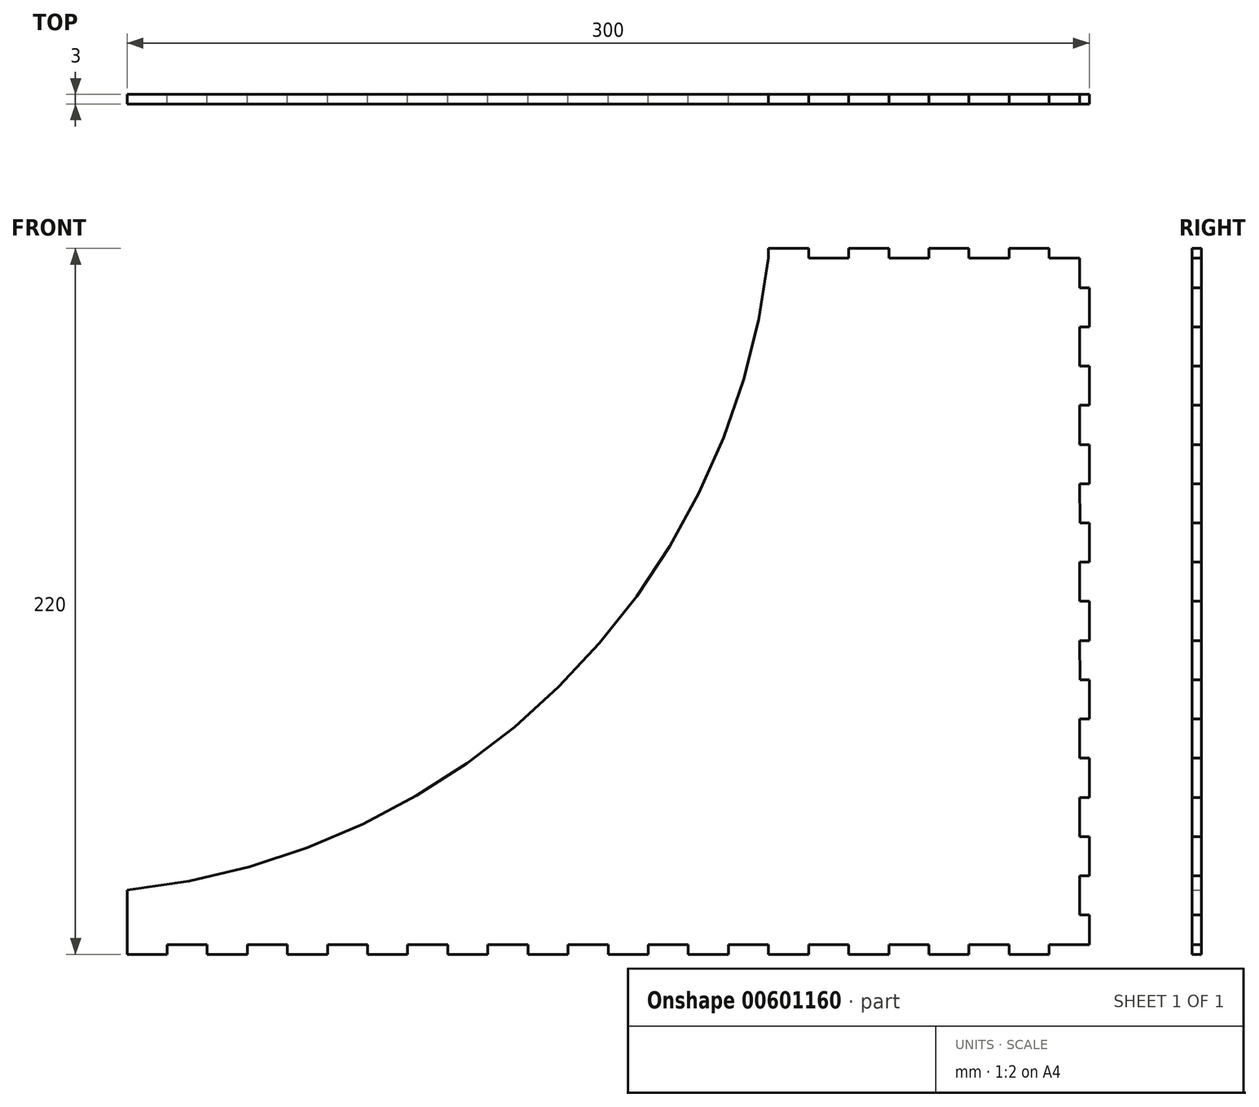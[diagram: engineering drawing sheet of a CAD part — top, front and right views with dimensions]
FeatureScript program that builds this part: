
annotation { "Feature Type Name" : "Feature", "Feature Type Description" : "" }
export const myFeature = defineFeature(function(context is Context, id is Id, definition is map)
    precondition{}
    {
        {
            var Q0;
            Q0=qCreatedBy(makeId("Front.planeOp"),FACE);
            var sketch = newSketch(context, id + "F0", { "sketchPlane" : qUnion([Q0])});
            skLineSegment(sketch, "E0.bottom", {"start": v(137.5, -110) * mm, "end": v(125, -110) * mm});
            skLineSegment(sketch, "E0.top", {"start": v(137.5, 110) * mm, "end": v(125, 110) * mm});
            skLineSegment(sketch, "E0.left", {"start": v(150, -107) * mm, "end": v(150, -97.78) * mm});
            skLineSegment(sketch, "E0.right", {"start": v(-150, -110) * mm, "end": v(-150, -90) * mm});
            skPoint(sketch, "E0.middle", {"position": v(0, 0) * mm});
            skPoint(sketch, "E1.orphan", {"position": v(-150, 110) * mm});
            skLineSegment(sketch, "E2", {"start": v(-137.5, -107) * mm, "end": v(-125, -107) * mm});
            skLineSegment(sketch, "E3", {"start": v(-137.5, -107) * mm, "end": v(-137.5, -110) * mm});
            skLineSegment(sketch, "E4", {"start": v(-125, -107) * mm, "end": v(-125, -110) * mm});
            skLineSegment(sketch, "E5", {"start": v(-112.5, -107) * mm, "end": v(-112.5, -110) * mm});
            skLineSegment(sketch, "E6", {"start": v(-100, -107) * mm, "end": v(-100, -110) * mm});
            skLineSegment(sketch, "E7", {"start": v(-87.5, -107) * mm, "end": v(-87.5, -110) * mm});
            skLineSegment(sketch, "E8", {"start": v(-75, -107) * mm, "end": v(-75, -110) * mm});
            skLineSegment(sketch, "E9", {"start": v(-62.5, -107) * mm, "end": v(-62.5, -110) * mm});
            skLineSegment(sketch, "E10", {"start": v(-50, -107) * mm, "end": v(-50, -110) * mm});
            skLineSegment(sketch, "E11", {"start": v(-37.5, -107) * mm, "end": v(-37.5, -110) * mm});
            skLineSegment(sketch, "E12", {"start": v(-25, -107) * mm, "end": v(-25, -110) * mm});
            skLineSegment(sketch, "E13", {"start": v(-12.5, -107) * mm, "end": v(-12.5, -110) * mm});
            skLineSegment(sketch, "E14", {"start": v(0, -107) * mm, "end": v(0, -110) * mm});
            skLineSegment(sketch, "E15.MirrorCS", {"start": v(100, -107) * mm, "end": v(100, -110) * mm});
            skLineSegment(sketch, "E16.MirrorCS", {"start": v(12.5, -107) * mm, "end": v(12.5, -110) * mm});
            skLineSegment(sketch, "E17.MirrorCS", {"start": v(50, -107) * mm, "end": v(50, -110) * mm});
            skLineSegment(sketch, "E18.MirrorCS", {"start": v(25, -107) * mm, "end": v(25, -110) * mm});
            skLineSegment(sketch, "E19.MirrorCS", {"start": v(62.5, -107) * mm, "end": v(62.5, -110) * mm});
            skLineSegment(sketch, "E20.MirrorCS", {"start": v(37.5, -107) * mm, "end": v(37.5, -110) * mm});
            skLineSegment(sketch, "E21.MirrorCS", {"start": v(112.5, -107) * mm, "end": v(112.5, -110) * mm});
            skLineSegment(sketch, "E22.MirrorCS", {"start": v(87.5, -107) * mm, "end": v(87.5, -110) * mm});
            skLineSegment(sketch, "E23.MirrorCS", {"start": v(137.5, -107) * mm, "end": v(137.5, -110) * mm});
            skLineSegment(sketch, "E24.MirrorCS", {"start": v(125, -107) * mm, "end": v(125, -110) * mm});
            skLineSegment(sketch, "E25.MirrorCS", {"start": v(75, -107) * mm, "end": v(75, -110) * mm});
            skLineSegment(sketch, "E26.trimOffspring", {"start": v(-137.5, -110) * mm, "end": v(-150, -110) * mm});
            skLineSegment(sketch, "E27.trimOffspring", {"start": v(-112.5, -107) * mm, "end": v(-100, -107) * mm});
            skLineSegment(sketch, "E28.trimOffspring", {"start": v(-112.5, -110) * mm, "end": v(-125, -110) * mm});
            skLineSegment(sketch, "E29.trimOffspring", {"start": v(-87.5, -107) * mm, "end": v(-75, -107) * mm});
            skLineSegment(sketch, "E30.trimOffspring", {"start": v(-87.5, -110) * mm, "end": v(-100, -110) * mm});
            skLineSegment(sketch, "E31.trimOffspring", {"start": v(-62.5, -107) * mm, "end": v(-50, -107) * mm});
            skLineSegment(sketch, "E32.trimOffspring", {"start": v(-62.5, -110) * mm, "end": v(-75, -110) * mm});
            skLineSegment(sketch, "E33.trimOffspring", {"start": v(-37.5, -107) * mm, "end": v(-25, -107) * mm});
            skLineSegment(sketch, "E34.trimOffspring", {"start": v(-37.5, -110) * mm, "end": v(-50, -110) * mm});
            skLineSegment(sketch, "E35.trimOffspring", {"start": v(-12.5, -107) * mm, "end": v(0, -107) * mm});
            skLineSegment(sketch, "E36.trimOffspring", {"start": v(-12.5, -110) * mm, "end": v(-25, -110) * mm});
            skLineSegment(sketch, "E37.trimOffspring", {"start": v(12.5, -107) * mm, "end": v(25, -107) * mm});
            skLineSegment(sketch, "E38.trimOffspring", {"start": v(12.5, -110) * mm, "end": v(0, -110) * mm});
            skLineSegment(sketch, "E39.trimOffspring", {"start": v(37.5, -107) * mm, "end": v(50, -107) * mm});
            skLineSegment(sketch, "E40.trimOffspring", {"start": v(37.5, -110) * mm, "end": v(25, -110) * mm});
            skLineSegment(sketch, "E41.trimOffspring", {"start": v(62.5, -107) * mm, "end": v(75, -107) * mm});
            skLineSegment(sketch, "E42.trimOffspring", {"start": v(62.5, -110) * mm, "end": v(50, -110) * mm});
            skLineSegment(sketch, "E43.trimOffspring", {"start": v(87.5, -107) * mm, "end": v(100, -107) * mm});
            skLineSegment(sketch, "E44.trimOffspring", {"start": v(87.5, -110) * mm, "end": v(75, -110) * mm});
            skLineSegment(sketch, "E45.trimOffspring", {"start": v(112.5, -107) * mm, "end": v(125, -107) * mm});
            skLineSegment(sketch, "E46.trimOffspring", {"start": v(112.5, -110) * mm, "end": v(100, -110) * mm});
            skLineSegment(sketch, "E47.trimOffspring", {"start": v(137.5, -107) * mm, "end": v(150, -107) * mm});
            skPoint(sketch, "E48.orphan", {"position": v(150, -110) * mm});
            skLineSegment(sketch, "E49", {"start": v(147, 107) * mm, "end": v(137.5, 107) * mm});
            skArc(sketch, "E50", {"start": v(-150, -90) * mm, "mid": v(-15.4, -26.63) * mm, "end": v(50, 107) * mm});
            skLineSegment(sketch, "E51", {"start": v(50, 110) * mm, "end": v(50, 107) * mm});
            skLineSegment(sketch, "E52.MirrorCS", {"start": v(50, 107) * mm, "end": v(50, 110) * mm});
            skLineSegment(sketch, "E53.MirrorCS", {"start": v(137.5, 107) * mm, "end": v(137.5, 110) * mm});
            skLineSegment(sketch, "E54.MirrorCS", {"start": v(62.5, 107) * mm, "end": v(62.5, 110) * mm});
            skLineSegment(sketch, "E55.MirrorCS", {"start": v(125, 107) * mm, "end": v(125, 110) * mm});
            skLineSegment(sketch, "E56.MirrorCS", {"start": v(87.5, 107) * mm, "end": v(87.5, 110) * mm});
            skLineSegment(sketch, "E57.MirrorCS", {"start": v(100, 107) * mm, "end": v(100, 110) * mm});
            skLineSegment(sketch, "E58.MirrorCS", {"start": v(75, 107) * mm, "end": v(75, 110) * mm});
            skLineSegment(sketch, "E59.MirrorCS", {"start": v(112.5, 107) * mm, "end": v(112.5, 110) * mm});
            skLineSegment(sketch, "E60.MirrorCS", {"start": v(137.5, 107) * mm, "end": v(147, 107) * mm});
            skLineSegment(sketch, "E61.MirrorCS", {"start": v(87.5, 110) * mm, "end": v(75, 110) * mm});
            skPoint(sketch, "E62.MirrorP", {"position": v(150, 110) * mm});
            skLineSegment(sketch, "E63.MirrorCS", {"start": v(112.5, 107) * mm, "end": v(125, 107) * mm});
            skLineSegment(sketch, "E64.MirrorCS", {"start": v(87.5, 107) * mm, "end": v(100, 107) * mm});
            skLineSegment(sketch, "E65.MirrorCS", {"start": v(62.5, 107) * mm, "end": v(75, 107) * mm});
            skLineSegment(sketch, "E66.MirrorCS", {"start": v(112.5, 110) * mm, "end": v(100, 110) * mm});
            skLineSegment(sketch, "E67.MirrorCS", {"start": v(62.5, 110) * mm, "end": v(50, 110) * mm});
            skLineSegment(sketch, "E68.trimOffspring", {"start": v(125, 107) * mm, "end": v(112.5, 107) * mm});
            skLineSegment(sketch, "E69.trimOffspring", {"start": v(100, 107) * mm, "end": v(87.5, 107) * mm});
            skLineSegment(sketch, "E70.trimOffspring", {"start": v(75, 107) * mm, "end": v(62.5, 107) * mm});
            skLineSegment(sketch, "E71", {"start": v(147, 107) * mm, "end": v(147, 97.78) * mm});
            skLineSegment(sketch, "E72", {"start": v(147, 97.78) * mm, "end": v(150, 97.78) * mm});
            skLineSegment(sketch, "E73", {"start": v(147, 85.56) * mm, "end": v(150, 85.56) * mm});
            skLineSegment(sketch, "E74", {"start": v(147, 73.33) * mm, "end": v(150, 73.33) * mm});
            skLineSegment(sketch, "E75", {"start": v(147, 61.11) * mm, "end": v(150, 61.11) * mm});
            skLineSegment(sketch, "E76", {"start": v(147, 48.9) * mm, "end": v(150, 48.9) * mm});
            skLineSegment(sketch, "E77", {"start": v(147, 36.67) * mm, "end": v(150, 36.67) * mm});
            skLineSegment(sketch, "E78", {"start": v(147.08, 24.45) * mm, "end": v(150, 24.45) * mm});
            skLineSegment(sketch, "E79", {"start": v(147, 12.22) * mm, "end": v(150, 12.22) * mm});
            skLineSegment(sketch, "E80", {"start": v(147, 0) * mm, "end": v(150, 0) * mm});
            skLineSegment(sketch, "E81.MirrorCS", {"start": v(147, -36.67) * mm, "end": v(150, -36.67) * mm});
            skLineSegment(sketch, "E82.MirrorCS", {"start": v(147.08, -24.45) * mm, "end": v(150, -24.45) * mm});
            skLineSegment(sketch, "E83.MirrorCS", {"start": v(147, -12.22) * mm, "end": v(150, -12.22) * mm});
            skLineSegment(sketch, "E84.MirrorCS", {"start": v(147, -97.78) * mm, "end": v(150, -97.78) * mm});
            skLineSegment(sketch, "E85.MirrorCS", {"start": v(147, -48.9) * mm, "end": v(150, -48.9) * mm});
            skLineSegment(sketch, "E86.MirrorCS", {"start": v(147, -61.11) * mm, "end": v(150, -61.11) * mm});
            skLineSegment(sketch, "E87.MirrorCS", {"start": v(147, -85.56) * mm, "end": v(150, -85.56) * mm});
            skLineSegment(sketch, "E88.MirrorCS", {"start": v(147, -73.33) * mm, "end": v(150, -73.33) * mm});
            skPoint(sketch, "E89.orphan", {"position": v(150, 107) * mm});
            skLineSegment(sketch, "E90.trimOffspring", {"start": v(147, 85.56) * mm, "end": v(147, 73.33) * mm});
            skLineSegment(sketch, "E91.trimOffspring", {"start": v(150, 85.56) * mm, "end": v(150, 97.78) * mm});
            skLineSegment(sketch, "E92.trimOffspring", {"start": v(147, 61.11) * mm, "end": v(147, 48.9) * mm});
            skLineSegment(sketch, "E93.trimOffspring", {"start": v(150, 61.11) * mm, "end": v(150, 73.33) * mm});
            skLineSegment(sketch, "E94.trimOffspring", {"start": v(147, 12.22) * mm, "end": v(147, 0) * mm});
            skLineSegment(sketch, "E95.trimOffspring", {"start": v(150, 36.67) * mm, "end": v(150, 48.9) * mm});
            skLineSegment(sketch, "E96", {"start": v(147.08, 24.45) * mm, "end": v(147, 36.67) * mm});
            skLineSegment(sketch, "E97.trimOffspring", {"start": v(150, 12.22) * mm, "end": v(150, 24.45) * mm});
            skLineSegment(sketch, "E98.trimOffspring", {"start": v(147, -36.67) * mm, "end": v(147, -48.9) * mm});
            skLineSegment(sketch, "E99.trimOffspring", {"start": v(150, -12.22) * mm, "end": v(150, 0) * mm});
            skLineSegment(sketch, "E100", {"start": v(147, -12.22) * mm, "end": v(147.08, -24.45) * mm});
            skLineSegment(sketch, "E101.trimOffspring", {"start": v(150, -36.67) * mm, "end": v(150, -24.45) * mm});
            skLineSegment(sketch, "E102.trimOffspring", {"start": v(147, -61.11) * mm, "end": v(147, -73.33) * mm});
            skLineSegment(sketch, "E103.trimOffspring", {"start": v(150, -61.11) * mm, "end": v(150, -48.9) * mm});
            skLineSegment(sketch, "E104.trimOffspring", {"start": v(147, -85.56) * mm, "end": v(147, -97.78) * mm});
            skLineSegment(sketch, "E105.trimOffspring", {"start": v(150, -85.56) * mm, "end": v(150, -73.33) * mm});
            skSolve(sketch);
        }
        {
            var Q0;
            Q0=makeQuery(id+"F0.imprint","IMPRINT",FACE,{"disambiguationData":[TD([[makeQuery(id+"F0.imprint","IMPRINT",EDGE,{"derivedFrom":sQuery(id+"F0.wireOp",EDGE,"E0.bottom")}),-1.0]])]});
            extrude(context, id + "F1", {"entities" : qUnion([Q0]), "depth" : 3 * mm, "offsetDistance" : 25 * mm});
        }
    });
